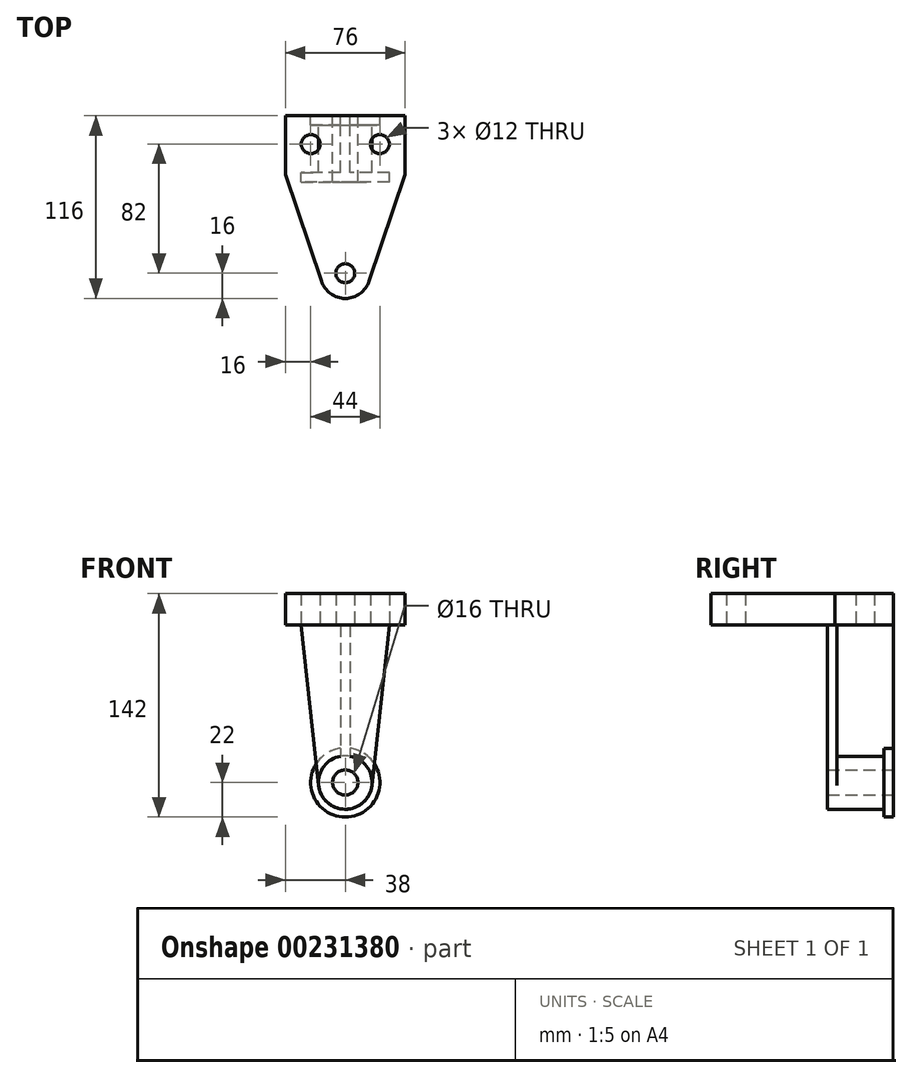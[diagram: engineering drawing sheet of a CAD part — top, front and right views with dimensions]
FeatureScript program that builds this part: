
annotation { "Feature Type Name" : "Feature", "Feature Type Description" : "" }
export const myFeature = defineFeature(function(context is Context, id is Id, definition is map)
    precondition{}
    {
        {
            var Q0;
            Q0=qCreatedBy(makeId("Front.planeOp"),FACE);
            var sketch = newSketch(context, id + "F0", { "sketchPlane" : qUnion([Q0])});
            skCircle(sketch, "E0", {"center": v(0, 0) * mm, "radius": 8 * mm});
            skCircle(sketch, "E1", {"center": v(0, 0) * mm, "radius": 22 * mm});
            skLineSegment(sketch, "E2", {"start": v(-38, 120) * mm, "end": v(38, 120) * mm});
            skLineSegment(sketch, "E3", {"start": v(38, 120) * mm, "end": v(38, 100) * mm});
            skLineSegment(sketch, "E4", {"start": v(38, 100) * mm, "end": v(-38, 100) * mm});
            skLineSegment(sketch, "E5", {"start": v(-38, 100) * mm, "end": v(-38, 120) * mm});
            skLineSegment(sketch, "E6", {"start": v(-3, 100) * mm, "end": v(-3, 21.8) * mm});
            skLineSegment(sketch, "E7", {"start": v(3, 100) * mm, "end": v(3, 21.8) * mm});
            skCircle(sketch, "E8", {"center": v(0, 0) * mm, "radius": 17 * mm});
            skLineSegment(sketch, "E9", {"start": v(-3, 21.8) * mm, "end": v(-3, 16.73) * mm});
            skLineSegment(sketch, "E10", {"start": v(3, 21.8) * mm, "end": v(3, 16.73) * mm});
            skSolve(sketch);
        }
        {
            var Q0;
            Q0=makeQuery(id+"F0.imprint","IMPRINT",FACE,{"disambiguationData":[TD([[makeQuery(id+"F0.imprint","IMPRINT",EDGE,{"derivedFrom":sQuery(id+"F0.wireOp",EDGE,"E0")}),-1.0]])]});
            extrude(context, id + "F1", {"entities" : qUnion([Q0]), "depth" : 40 * mm});
        }
        {
            var Q0;
            {var subQ0=sQuery(id+"F0.wireOp",EDGE,"E9");Q0=makeQuery(id+"F0.imprint","IMPRINT",FACE,{"disambiguationData":[TD([[makeQuery(id+"F0.imprint","IMPRINT",EDGE,{"derivedFrom":subQ0}),-1.0]])]});}
            extrude(context, id + "F2", {"entities" : qUnion([Q0]), "operationType" : NewBodyOperationType.ADD, "depth" : 6 * mm});
        }
        {
            var Q0;
            {var subQ0=sQuery(id+"F0.wireOp",EDGE,"E9");Q0=makeQuery(id+"F0.imprint","IMPRINT",FACE,{"disambiguationData":[TD([[makeQuery(id+"F0.imprint","IMPRINT",EDGE,{"derivedFrom":subQ0}),1.0]])]});}
            var Q1;
            {var subQ0=sQuery(id+"F0.wireOp",EDGE,"E6");Q1=makeQuery(id+"F0.imprint","IMPRINT",FACE,{"disambiguationData":[TD([[makeQuery(id+"F0.imprint","IMPRINT",EDGE,{"derivedFrom":subQ0}),1.0]])]});}
            extrude(context, id + "F3", {"entities" : qUnion([Q0, Q1]), "operationType" : NewBodyOperationType.ADD, "depth" : 40 * mm});
        }
        {
            var Q0;
            Q0=makeQuery(id+"F0.imprint","IMPRINT",FACE,{"disambiguationData":[TD([[makeQuery(id+"F0.imprint","IMPRINT",EDGE,{"derivedFrom":sQuery(id+"F0.wireOp",EDGE,"E2")}),-1.0]])]});
            extrude(context, id + "F4", {"entities" : qUnion([Q0]), "operationType" : NewBodyOperationType.ADD, "depth" : 116 * mm});
        }
        {
            var Q0;
            Q0=makeQuery(id+"F4.opExtrude","SWEPT_FACE",FACE,{"disambiguationData":[OSD([sQuery(id+"F0.wireOp",EDGE,"E4")])]});
            var sketch = newSketch(context, id + "F5", { "sketchPlane" : qUnion([Q0])});
            skCircle(sketch, "E11", {"center": v(-22, 18) * mm, "radius": 6 * mm});
            skCircle(sketch, "E12", {"center": v(22, 18) * mm, "radius": 6 * mm});
            skSolve(sketch);
        }
        {
            var Q0;
            Q0=qSketchRegion(id+"F5",true);
            extrude(context, id + "F6", {"entities" : qUnion([Q0]), "operationType" : NewBodyOperationType.REMOVE, "oppositeDirection" : true, "depth" : 20 * mm});
        }
        {
            var Q0;
            Q0=makeQuery(id+"F0.imprint","IMPRINT",FACE,{"disambiguationData":[TD([[makeQuery(id+"F0.imprint","IMPRINT",EDGE,{"derivedFrom":sQuery(id+"F0.wireOp",EDGE,"E2")}),-1.0]])]});
            cPlane(context, id + "F7", {"entities" : qUnion([Q0]), "cplaneType" : CPlaneType.OFFSET, "offset" : 36 * mm, "width" : 150 * mm, "height" : 150 * mm});
        }
        {
            var Q0;
            Q0=qCreatedBy(id+"F7.planeOp",FACE);
            var sketch = newSketch(context, id + "F8", { "sketchPlane" : qUnion([Q0])});
            skCircle(sketch, "E13.0", {"center": v(0, 0) * mm, "radius": 17 * mm});
            skLineSegment(sketch, "E14.0", {"start": v(38, 100) * mm, "end": v(-38, 100) * mm});
            skLineSegment(sketch, "E15", {"start": v(-28, 100) * mm, "end": v(-16.9, -1.84) * mm});
            skLineSegment(sketch, "E16.0", {"start": v(-3, 100) * mm, "end": v(-3, 21.8) * mm});
            skLineSegment(sketch, "E17", {"start": v(0, -34.15) * mm, "end": v(0, 148.38) * mm});
            skLineSegment(sketch, "E18.MirrorCS", {"start": v(28, 100) * mm, "end": v(16.9, -1.84) * mm});
            skSolve(sketch);
        }
        {
            var Q0;
            Q0=qSketchRegion(id+"F8",true);
            extrude(context, id + "F9", {"entities" : qUnion([Q0]), "operationType" : NewBodyOperationType.ADD, "depth" : 6 * mm});
        }
        {
            var Q0;
            Q0=makeQuery(id+"F4.opExtrude","SWEPT_FACE",FACE,{"disambiguationData":[OSD([sQuery(id+"F0.wireOp",EDGE,"E4")])]});
            var sketch = newSketch(context, id + "F10", { "sketchPlane" : qUnion([Q0])});
            skCircle(sketch, "E19", {"center": v(0, 100) * mm, "radius": 16 * mm});
            skCircle(sketch, "E20", {"center": v(0, 100) * mm, "radius": 6 * mm});
            skLineSegment(sketch, "E21", {"start": v(15.16, 105.11) * mm, "end": v(38, 37.37) * mm});
            skLineSegment(sketch, "E22", {"start": v(0, 100) * mm, "end": v(0, -44.21) * mm});
            skLineSegment(sketch, "E23.MirrorCS", {"start": v(-15.16, 105.11) * mm, "end": v(-38, 37.37) * mm});
            skSolve(sketch);
        }
        {
            var Q0;
            Q0=makeQuery(id+"F10.imprint","IMPRINT",FACE,{"disambiguationData":[TD([[makeQuery(id+"F10.imprint","IMPRINT",EDGE,{"derivedFrom":sQuery(id+"F10.wireOp",EDGE,"E20")}),1.0]])]});
            extrude(context, id + "F11", {"entities" : qUnion([Q0]), "operationType" : NewBodyOperationType.REMOVE, "oppositeDirection" : true, "depth" : 20 * mm});
        }
        {
            var Q0;
            {var subQ0=sQuery(id+"F10.wireOp",EDGE,"E21");Q0=makeQuery(id+"F10.imprint","IMPRINT",FACE,{"disambiguationData":[TD([[makeQuery(id+"F10.imprint","IMPRINT",EDGE,{"derivedFrom":subQ0}),1.0]])]});}
            var Q1;
            {var subQ0=sQuery(id+"F10.wireOp",EDGE,"E23.MirrorCS");Q1=makeQuery(id+"F10.imprint","IMPRINT",FACE,{"disambiguationData":[TD([[makeQuery(id+"F10.imprint","IMPRINT",EDGE,{"derivedFrom":subQ0}),-1.0]])]});}
            extrude(context, id + "F12", {"entities" : qUnion([Q0, Q1]), "operationType" : NewBodyOperationType.REMOVE, "oppositeDirection" : true, "depth" : 20 * mm});
        }
        {
            var Q0;
            {var subQ0=sQuery(id+"F0.wireOp",EDGE,"E0");Q0=makeQuery(id+"F9.boolean.opBoolean","SPLIT",FACE,{"disambiguationData":[TD([makeQuery(id+"F1.opExtrude","SWEPT_FACE",FACE,{"disambiguationData":[OSD([subQ0])]})])],"derivedFrom":makeQuery(id+"F9.opExtrude","CAP_FACE",FACE,{"disambiguationData":[OSD([sQuery(id+"F8.wireOp",EDGE,"E13.0"),sQuery(id+"F8.wireOp",EDGE,"E14.0"),sQuery(id+"F8.wireOp",EDGE,"E15"),sQuery(id+"F8.wireOp",EDGE,"E18.MirrorCS")])],"isStart":true})});}
            extrude(context, id + "F13", {"entities" : qUnion([Q0]), "operationType" : NewBodyOperationType.REMOVE, "endBound" : BoundingType.THROUGH_ALL, "oppositeDirection" : true, "depth" : 25 * mm});
        }
    });
